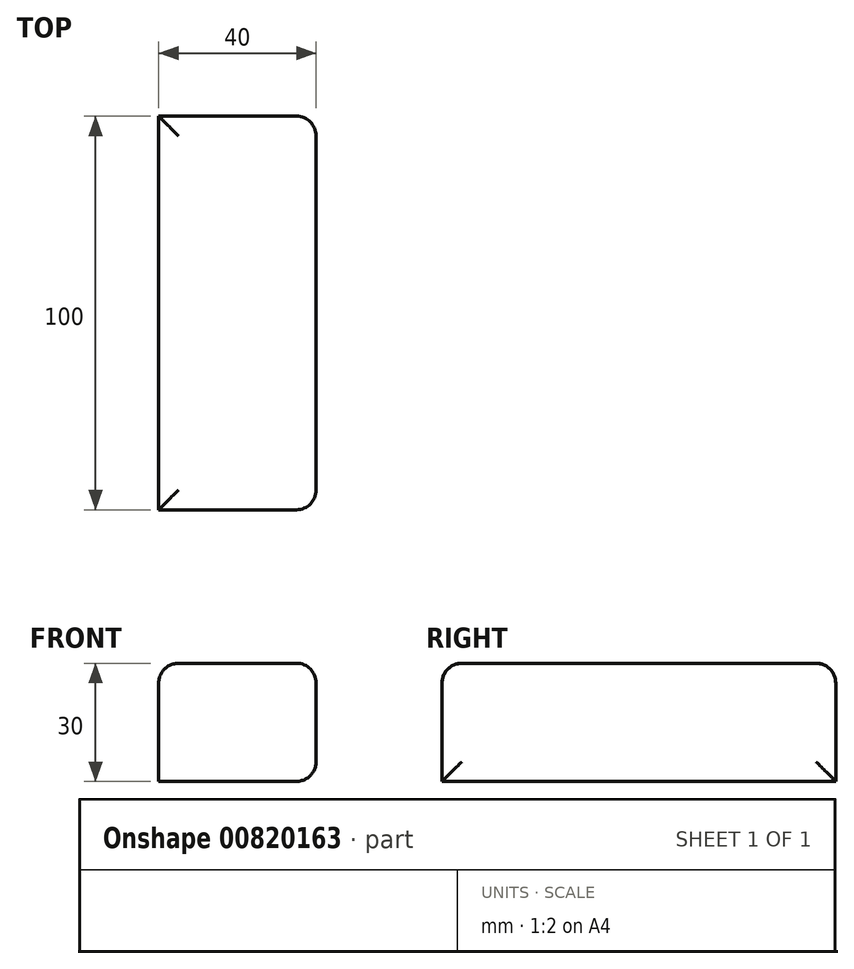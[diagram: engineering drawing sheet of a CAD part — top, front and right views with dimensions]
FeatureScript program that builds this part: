
annotation { "Feature Type Name" : "Feature", "Feature Type Description" : "" }
export const myFeature = defineFeature(function(context is Context, id is Id, definition is map)
    precondition{}
    {
        {
            var Q0;
            Q0=qCreatedBy(makeId("Front.planeOp"),FACE);
            var sketch = newSketch(context, id + "F0", { "sketchPlane" : qUnion([Q0])});
            skLineSegment(sketch, "E0.bottom", {"start": v(-24.82, 14.58) * mm, "end": v(15.18, 14.58) * mm});
            skLineSegment(sketch, "E0.top", {"start": v(-24.82, -15.42) * mm, "end": v(15.18, -15.42) * mm});
            skLineSegment(sketch, "E0.left", {"start": v(-24.82, 14.58) * mm, "end": v(-24.82, -15.42) * mm});
            skLineSegment(sketch, "E0.right", {"start": v(15.18, 14.58) * mm, "end": v(15.18, -15.42) * mm});
            skPoint(sketch, "E0.middle", {"position": v(-4.82, -0.42) * mm});
            skSolve(sketch);
        }
        {
            var Q0;
            Q0=makeQuery(id+"F0.imprint","IMPRINT",FACE,{"disambiguationData":[TD([[makeQuery(id+"F0.imprint","IMPRINT",EDGE,{"derivedFrom":sQuery(id+"F0.wireOp",EDGE,"E0.bottom")}),-1.0]])]});
            extrude(context, id + "F1", {"entities" : qUnion([Q0]), "endBound" : BoundingType.SYMMETRIC, "depth" : 100 * mm, "offsetDistance" : 25 * mm});
        }
        {
            var Q0;
            Q0=makeQuery(id+"F1.opExtrude","SWEPT_FACE",FACE,{"disambiguationData":[OSD([sQuery(id+"F0.wireOp",EDGE,"E0.bottom")])]});
            fillet(context, id + "F2", {"entities" : qUnion([Q0]), "radius" : 5 * mm, "tangentPropagation" : true, "allowEdgeOverflow" : false});
        }
        {
            var Q0;
            Q0=makeQuery(id+"F1.opExtrude","SWEPT_FACE",FACE,{"disambiguationData":[OSD([sQuery(id+"F0.wireOp",EDGE,"E0.right")])]});
            fillet(context, id + "F3", {"entities" : qUnion([Q0]), "radius" : 5 * mm, "tangentPropagation" : true, "allowEdgeOverflow" : false});
        }
    });
